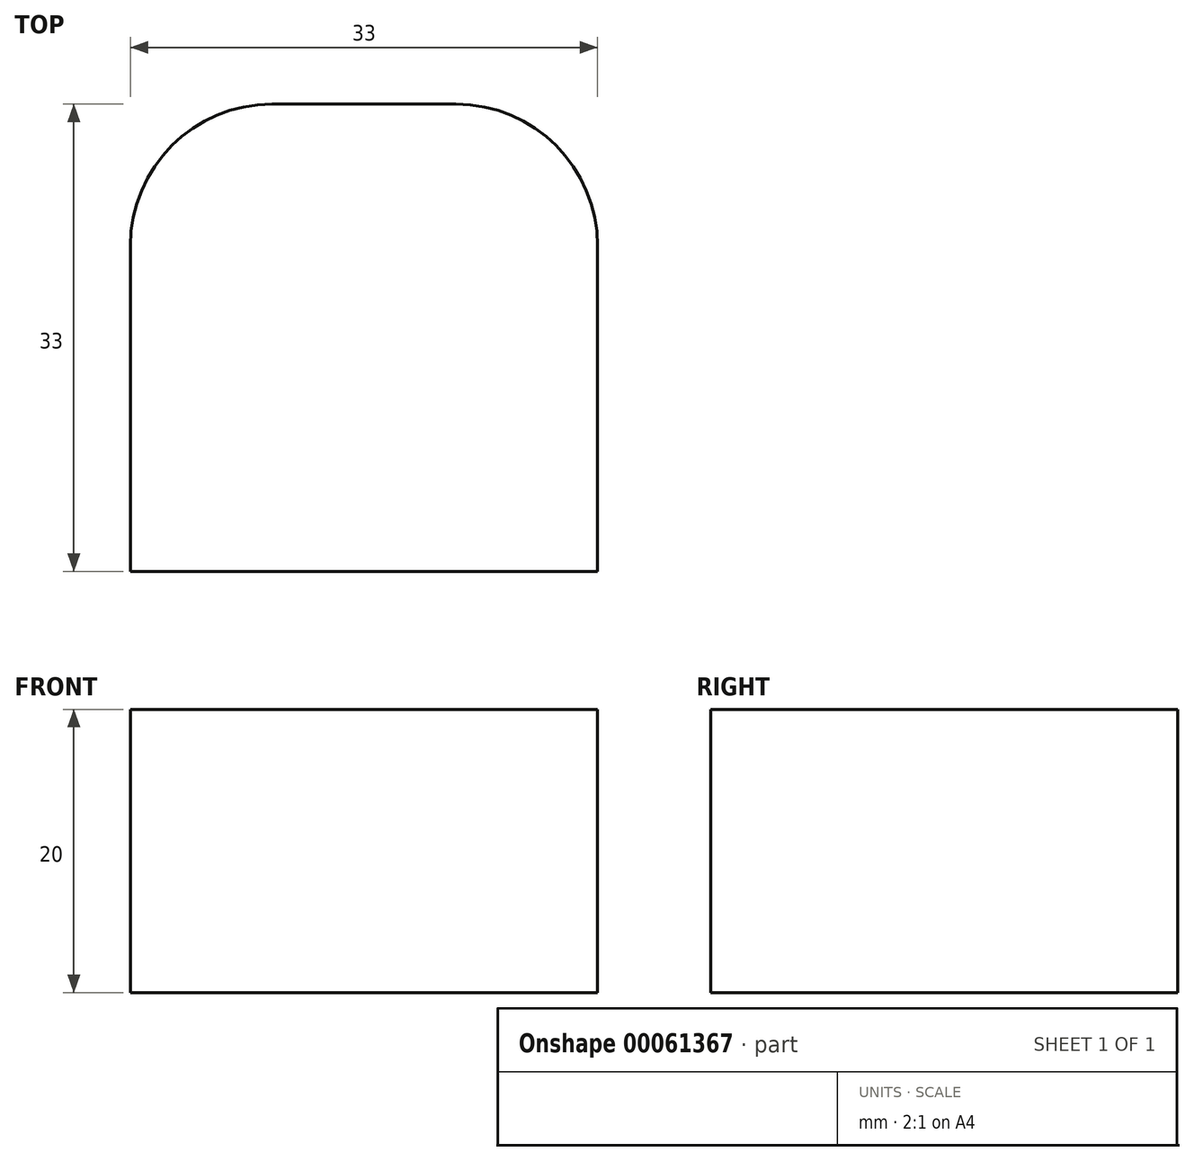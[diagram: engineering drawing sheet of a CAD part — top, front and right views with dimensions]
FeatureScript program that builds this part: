
annotation { "Feature Type Name" : "Feature", "Feature Type Description" : "" }
export const myFeature = defineFeature(function(context is Context, id is Id, definition is map)
    precondition{}
    {
        {
            var Q0;
            Q0=qCreatedBy(makeId("Top.planeOp"),FACE);
            var sketch = newSketch(context, id + "F0", { "sketchPlane" : qUnion([Q0])});
            skLineSegment(sketch, "E0.rect.bottom", {"start": v(16.5, 16.5) * mm, "end": v(-16.5, 16.5) * mm});
            skLineSegment(sketch, "E0.rect.top", {"start": v(16.5, -16.5) * mm, "end": v(-16.5, -16.5) * mm});
            skLineSegment(sketch, "E0.rect.left", {"start": v(16.5, 16.5) * mm, "end": v(16.5, -16.5) * mm});
            skLineSegment(sketch, "E0.rect.right", {"start": v(-16.5, 16.5) * mm, "end": v(-16.5, -16.5) * mm});
            skPoint(sketch, "E0.rect.middle", {"position": v(0, 0) * mm});
            skSolve(sketch);
        }
        {
            var Q0;
            Q0=makeQuery(id+"F0.imprint","IMPRINT",FACE,{"disambiguationData":[TD([[makeQuery(id+"F0.imprint","IMPRINT",EDGE,{"derivedFrom":sQuery(id+"F0.wireOp",EDGE,"E0.rect.bottom")}),1.0]])]});
            extrude(context, id + "F1", {"entities" : qUnion([Q0]), "depth" : 20 * mm});
        }
        {
            var Q0;
            Q0=makeQuery(id+"F1.opExtrude","SWEPT_EDGE",EDGE,{"disambiguationData":[OSD([sQuery(id+"F0.wireOp",EDGE,"E0.rect.bottom"),sQuery(id+"F0.wireOp",EDGE,"E0.rect.left")])]});
            var Q1;
            Q1=makeQuery(id+"F1.opExtrude","SWEPT_EDGE",EDGE,{"disambiguationData":[OSD([sQuery(id+"F0.wireOp",EDGE,"E0.rect.bottom"),sQuery(id+"F0.wireOp",EDGE,"E0.rect.right")])]});
            fillet(context, id + "F2", {"entities" : qUnion([Q0, Q1]), "radius" : 10 * mm, "tangentPropagation" : true, "allowEdgeOverflow" : false});
        }
    });
